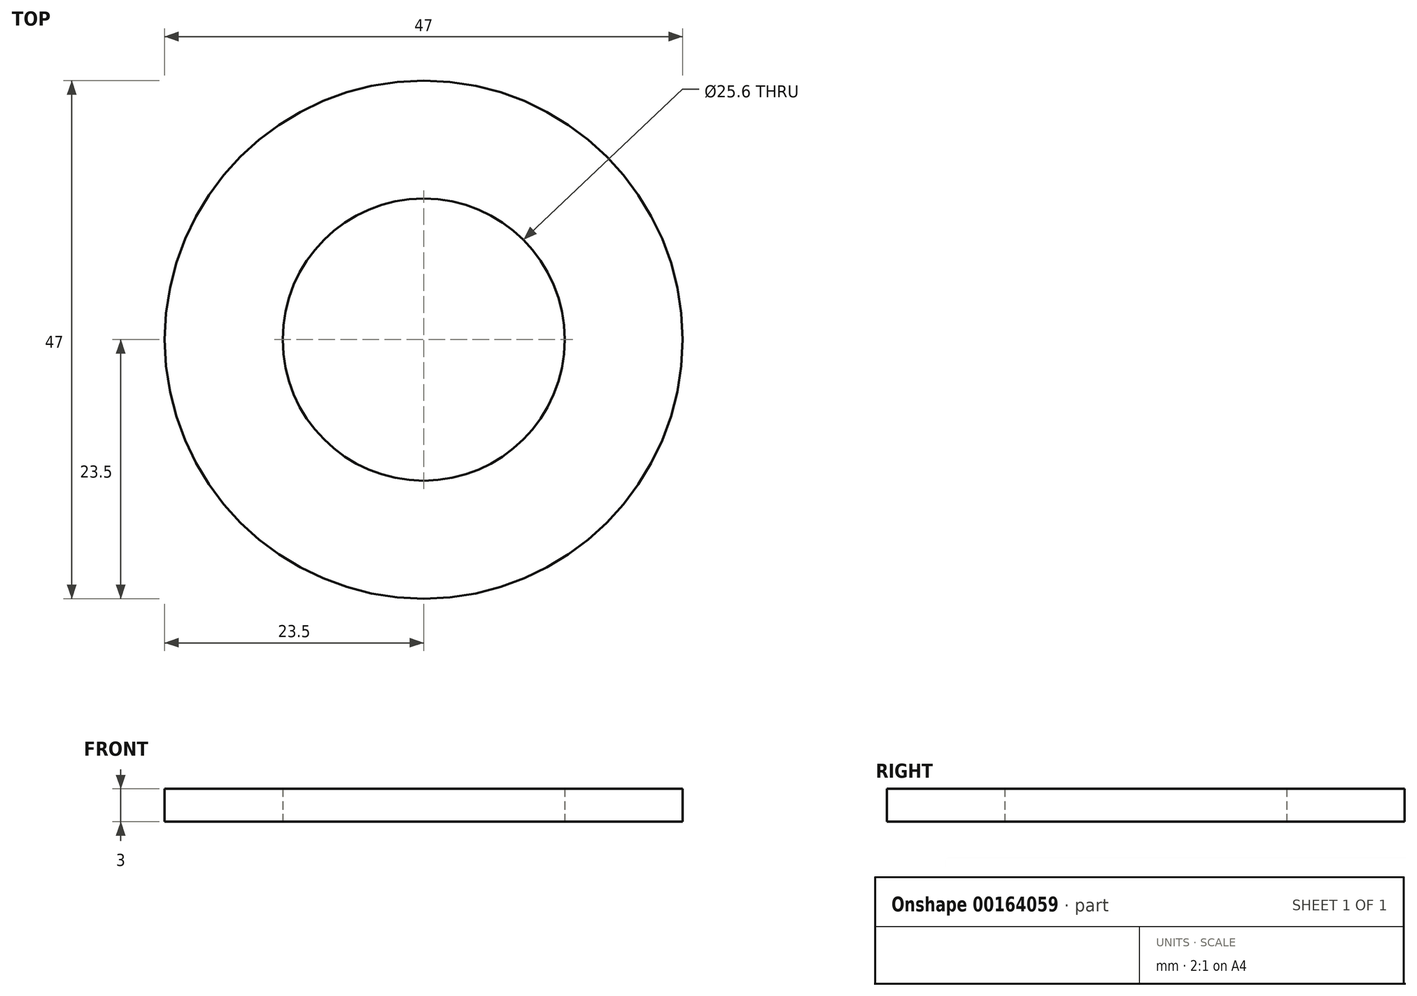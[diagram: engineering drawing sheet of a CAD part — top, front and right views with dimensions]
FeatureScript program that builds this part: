
annotation { "Feature Type Name" : "Feature", "Feature Type Description" : "" }
export const myFeature = defineFeature(function(context is Context, id is Id, definition is map)
    precondition{}
    {
        {
            var Q0;
            Q0=qCreatedBy(makeId("Top.planeOp"),FACE);
            var sketch = newSketch(context, id + "F0", { "sketchPlane" : qUnion([Q0])});
            skCircle(sketch, "E0", {"center": v(0, 0) * mm, "radius": 12.8 * mm});
            skCircle(sketch, "E1", {"center": v(0, 0) * mm, "radius": 23.5 * mm});
            skSolve(sketch);
        }
        {
            var Q0;
            Q0 = qSketchRegion(id + "F0", true);
            extrude(context, id + "F1", {"entities" : qUnion([Q0]), "depth" : 3 * mm});
        }
    });
